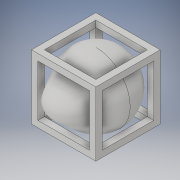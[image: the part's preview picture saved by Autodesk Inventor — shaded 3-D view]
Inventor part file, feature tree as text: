
AUTODESK INVENTOR PART (.ipt)
format: ipt  version: 2019 (Build 230136000, 136)  size: 501,248 bytes
history: native  units: mm
features: sketch x4, extrude x4, plane x1, other x1
ambient origin geometry x8: Origin, YZ Plane, XZ Plane, XY Plane, X Axis, Y Axis, Z Axis, Center Point
bodies: Solid1 (feature_tree), Solid2 (feature_tree)
feature tree (10):
  sketch  "Sketch1"  dims[d0=0.1mm d1=0.1mm]
  extrude  "Extrusion1"  Depth=0.1mm
  extrude  "Extrusion2"  Depth=0.01mm
  extrude  "Extrusion3"  Depth=0.08mm
  extrude  "Extrusion4"  Depth=0.1mm TaperAngle=0.0deg
  plane  "Work Plane1"
  sketch  "Sketch4"  dims[d7=0.08mm d8=0.1mm d9=0.0mm d10=0.08mm d12=0.01mm d13=0.1mm d14=0.0mm d15=0.01mm d16=0.01mm d17=0.08mm d18=0.08mm d19=0.1mm d20=0.0mm d21=-0.05mm]
  other  "Form1"
  sketch  "Sketch2"  dims[d2=0.1mm d3=0.0mm d4=0.01mm]
  sketch  "Sketch3"  dims[d5=0.01mm d6=0.08mm]
